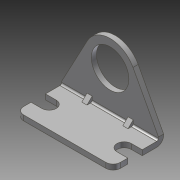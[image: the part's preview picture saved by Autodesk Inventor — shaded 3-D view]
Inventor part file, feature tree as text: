
AUTODESK INVENTOR PART (.ipt)
format: ipt  version: 2014 SP1 (Build 180222100, 222)  size: 208,896 bytes
history: native  units: in
note: dims shown in document units (in); Inventor stores cm internally (conversion verified against a paired STEP export)
features: other x126, sketch x5, extrude x4, hole x1, fillet x1, plane x1, mirror x1, projected_geometry x1
ambient origin geometry x8: Origin, YZ Plane, XZ Plane, XY Plane, X Axis, Y Axis, Z Axis, Center Point
bodies: Solid1 (feature_tree)
feature tree (140):
  extrude  "Extrusion1"  Depth=1.675in TaperAngle=0.0deg
  extrude  "Extrusion2"  Depth=0.25in TaperAngle=0.0deg
  hole  "Drilling 1"  [1 undecoded]
  extrude  "Extrusion5"  Depth=0.45in
  extrude  "Extrusion7"  Depth=0.875in
  other  "h1_XY"
  other  "h1_YZ"
  other  "h1_ZX"
  other  "h1_X"
  other  "h1_Y"
  other  "h1_Z"
  other  "h1_Center"
  other  "d1_XY"
  other  "d1_YZ"
  other  "d1_ZX"
  other  "d1_X"
  other  "d1_Y"
  other  "d1_Z"
  other  "d1_Center"
  other  "h2_XY"
  other  "h2_YZ"
  other  "h2_ZX"
  other  "h2_X"
  other  "h2_Y"
  other  "h2_Z"
  other  "h2_Center"
  other  "d2_XY"
  other  "d2_YZ"
  other  "d2_ZX"
  other  "d2_X"
  other  "d2_Y"
  other  "d2_Z"
  other  "d2_Center"
  other  "h3_XY"
  other  "h3_YZ"
  other  "h3_ZX"
  other  "h3_X"
  other  "h3_Y"
  other  "h3_Z"
  other  "h3_Center"
  other  "h4_XY"
  other  "h4_YZ"
  other  "h4_ZX"
  other  "h4_X"
  other  "h4_Y"
  other  "h4_Z"
  other  "h4_Center"
  other  "h5_XY"
  other  "h5_YZ"
  other  "h5_ZX"
  other  "h5_X"
  other  "h5_Y"
  other  "h5_Z"
  other  "h5_Center"
  other  "h6_XY"
  other  "h6_YZ"
  other  "h6_ZX"
  other  "h6_X"
  other  "h6_Y"
  other  "h6_Z"
  other  "h6_Center"
  other  "l1_XY"
  other  "l1_YZ"
  other  "l1_ZX"
  other  "l1_X"
  other  "l1_Y"
  other  "l1_Z"
  other  "l1_Center"
  other  "l2_XY"
  other  "l2_YZ"
  other  "l2_ZX"
  other  "l2_X"
  other  "l2_Y"
  other  "l2_Z"
  other  "l2_Center"
  other  "l3_XY"
  other  "l3_YZ"
  other  "l3_ZX"
  other  "l3_X"
  other  "l3_Y"
  other  "l3_Z"
  other  "l3_Center"
  other  "l4_XY"
  other  "l4_YZ"
  other  "l4_ZX"
  other  "l4_X"
  other  "l4_Y"
  other  "l4_Z"
  other  "l4_Center"
  other  "l5_XY"
  other  "l5_YZ"
  other  "l5_ZX"
  other  "l5_X"
  other  "l5_Y"
  other  "l5_Z"
  other  "l5_Center"
  other  "l6_XY"
  other  "l6_YZ"
  other  "l6_ZX"
  other  "l6_X"
  other  "l6_Y"
  other  "l6_Z"
  other  "l6_Center"
  other  "l7_XY"
  other  "l7_YZ"
  other  "l7_ZX"
  other  "l7_X"
  other  "l7_Y"
  other  "l7_Z"
  other  "l7_Center"
  other  "l8_XY"
  other  "l8_YZ"
  other  "l8_ZX"
  other  "l8_X"
  other  "l8_Y"
  other  "l8_Z"
  other  "l8_Center"
  other  "mounting_bracket_XY"
  other  "mounting_bracket_YZ"
  other  "mounting_bracket_ZX"
  other  "mounting_bracket_X"
  other  "mounting_bracket_Y"
  other  "mounting_bracket_Z"
  other  "mounting_bracket_Center"
  other  "mounting_bracket_1_XY"
  other  "mounting_bracket_1_YZ"
  other  "mounting_bracket_1_ZX"
  other  "mounting_bracket_1_X"
  other  "mounting_bracket_1_Y"
  other  "mounting_bracket_1_Z"
  other  "mounting_bracket_1_Center"
  fillet  "Fillet1"  Radius=0.0829in
  plane  "Work Plane56"
  mirror  "Mirror2"
  sketch  "Sketch_1"  dims[d0=1.675in d1=0.0in d2=0.1346in d3=0.0in]
  sketch  "Sketch_2"  dims[d4=0.65in d5=0.75in d6=0.375in d7=0.25in d8=0.5635in d9=0.1346in d10=0.0in d15=0.1346in d16=0.0in]
  sketch  "Sketch3"  dims[d19=0.0897in d20=0.0in d23=1.825in]
  sketch  "Sketch_8"  dims[d24=0.45in d25=0.75in]
  sketch  "Sketch_10"  dims[d26=1.4093in d27=1.925in d30=0.0829in d31=0.1375in d32=0.325in d33=0.125in d34=0.25in d35=0.25in d36=1.125in d37=0.1207in d38=0.031in d40=0.0897in d42=0.125in d43=0.875in]
  projected_geometry  "Projected Loop1"
note: 1 required parameter value undecoded (feature->parameter linkage not recoverable at this tier; creation-order binding heuristic only, values carry confidence <= 0.55)
